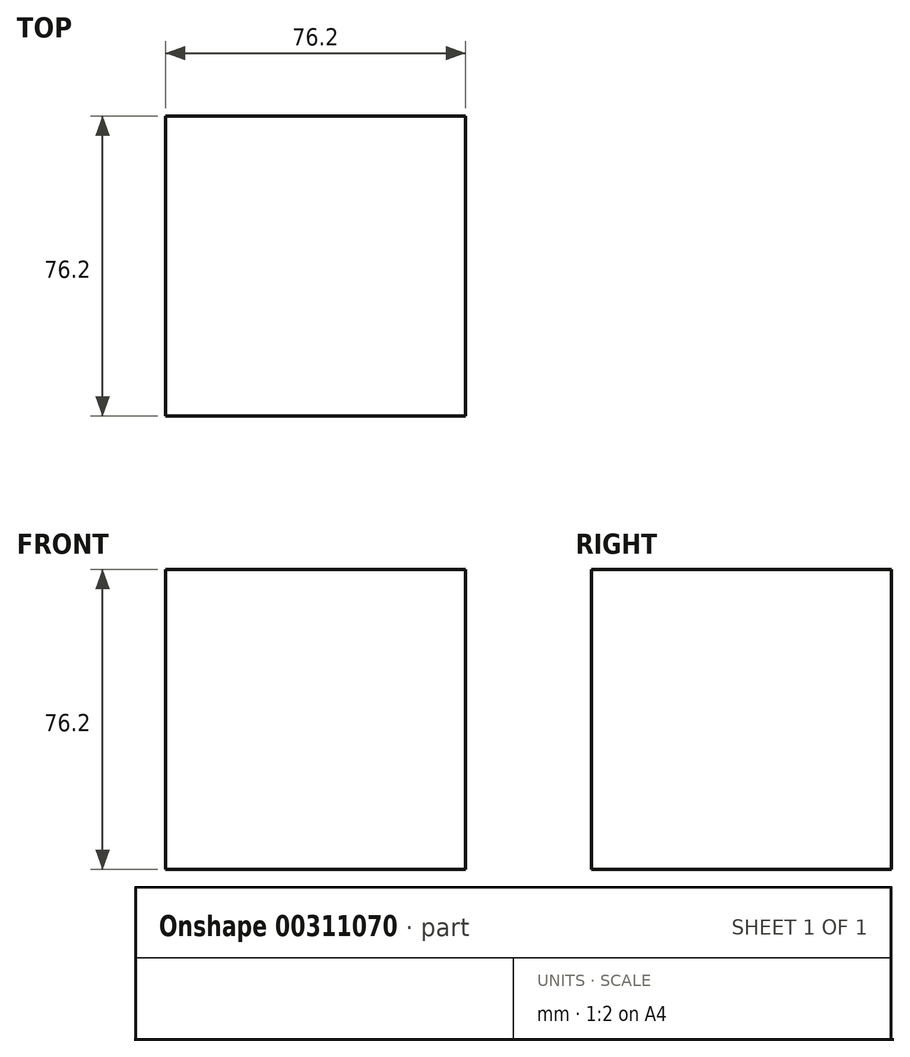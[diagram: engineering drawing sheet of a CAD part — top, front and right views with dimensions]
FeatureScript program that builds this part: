
annotation { "Feature Type Name" : "Feature", "Feature Type Description" : "" }
export const myFeature = defineFeature(function(context is Context, id is Id, definition is map)
    precondition{}
    {
        {
            var Q0;
            Q0=qCreatedBy(makeId("Front.planeOp"),FACE);
            var sketch = newSketch(context, id + "F0", { "sketchPlane" : qUnion([Q0])});
            skLineSegment(sketch, "E0.bottom", {"start": v(0, 0) * mm, "end": v(76.2, 0) * mm});
            skLineSegment(sketch, "E0.top", {"start": v(0, 76.2) * mm, "end": v(76.2, 76.2) * mm});
            skLineSegment(sketch, "E0.left", {"start": v(0, 0) * mm, "end": v(0, 76.2) * mm});
            skLineSegment(sketch, "E0.right", {"start": v(76.2, 0) * mm, "end": v(76.2, 76.2) * mm});
            skSolve(sketch);
        }
        {
            var Q0;
            Q0 = qSketchRegion(id + "F0", true);
            extrude(context, id + "F1", {"entities" : qUnion([Q0]), "depth" : 76.2 * mm});
        }
    });
